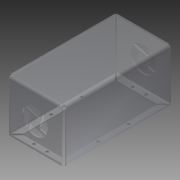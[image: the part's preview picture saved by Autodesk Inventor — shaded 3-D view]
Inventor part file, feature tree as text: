
AUTODESK INVENTOR PART (.ipt)
format: ipt  version: 2015 (Build 190159000, 159)  size: 494,592 bytes
history: native  units: in
note: dims shown in document units (in); Inventor stores cm internally (conversion verified against a paired STEP export)
features: sheet_metal_op x7, other x5, sketch x5, projected_geometry x5, hole x1, extrude x1, fillet x1
ambient origin geometry x8: Origin, YZ Plane, XZ Plane, XY Plane, X Axis, Y Axis, Z Axis, Center Point
bodies: Solid1 (feature_tree)
feature tree (25):
  sheet_metal_op  "Face1"
  sheet_metal_op  "Flange1"
  other  "A-Side Definition"
  sheet_metal_op  "Flange2"
  hole  "Hole1"  [1 undecoded]
  extrude  "Extrusion1"  Depth=0.125in
  fillet  "Fillet1"  Radius=0.0625in
  sketch  "Sketch1"  dims[d0=5.0in d1=10.0in]
  other  "Plate1"
  sketch  "Sketch2"  dims[d2=0.125in d3=0.125in d4=0.0625in]
  other  "Plate2"
  sheet_metal_op  "Bend1"
  sheet_metal_op  "Corner1"
  sketch  "Sketch3"  dims[d5=0.25in]
  other  "Plate3"
  sheet_metal_op  "Bend2"
  sheet_metal_op  "Corner2"
  sketch  "Sketch4"  dims[d6=0.125in]
  projected_geometry  "Projected Loop1"
  projected_geometry  "Projected Loop2"
  projected_geometry  "Projected Loop3"
  projected_geometry  "Projected Loop4"
  sketch  "Sketch5"  dims[d7=5.0in d8=90.0deg d9=0.125in d10=0.5in d11=0.125in d12=0.125in d13=0.125in d14=0.0625in d15=0.25in d16=0.125in d17=0.75in d18=90.0deg d19=0.125in d20=0.5in d21=0.125in d22=0.125in d23=0.5in d24=0.25in d25=0.25in d26=0.25in d27=0.25in d28=0.25in d29=0.25in d30=0.25in d31=0.25in d32=8.8232in d33=3.8232in d34=2.9411in d35=2.9411in d36=1.2744in d37=1.2744in d38=2.9411in d39=2.9411in d40=1.2744in d41=1.2744in d42=0.266in d43=0.75in d44=0.438in d45=0.25in d46=0.5635in d47=0.125in d48=0.8108in d49=5.0in d50=4.625in d51=2.5in d52=2.3125in d53=2.3622in d54=1.0in d55=0.0in d56=0.9843in d57=0.1969in d58=1.5748in d60=360.0deg d62=0.125in d63=0.0625in d64=1.2205in]
  projected_geometry  "Projected Loop5"
  other  "Definition1"
note: 1 required parameter value undecoded (feature->parameter linkage not recoverable at this tier; creation-order binding heuristic only, values carry confidence <= 0.55)
